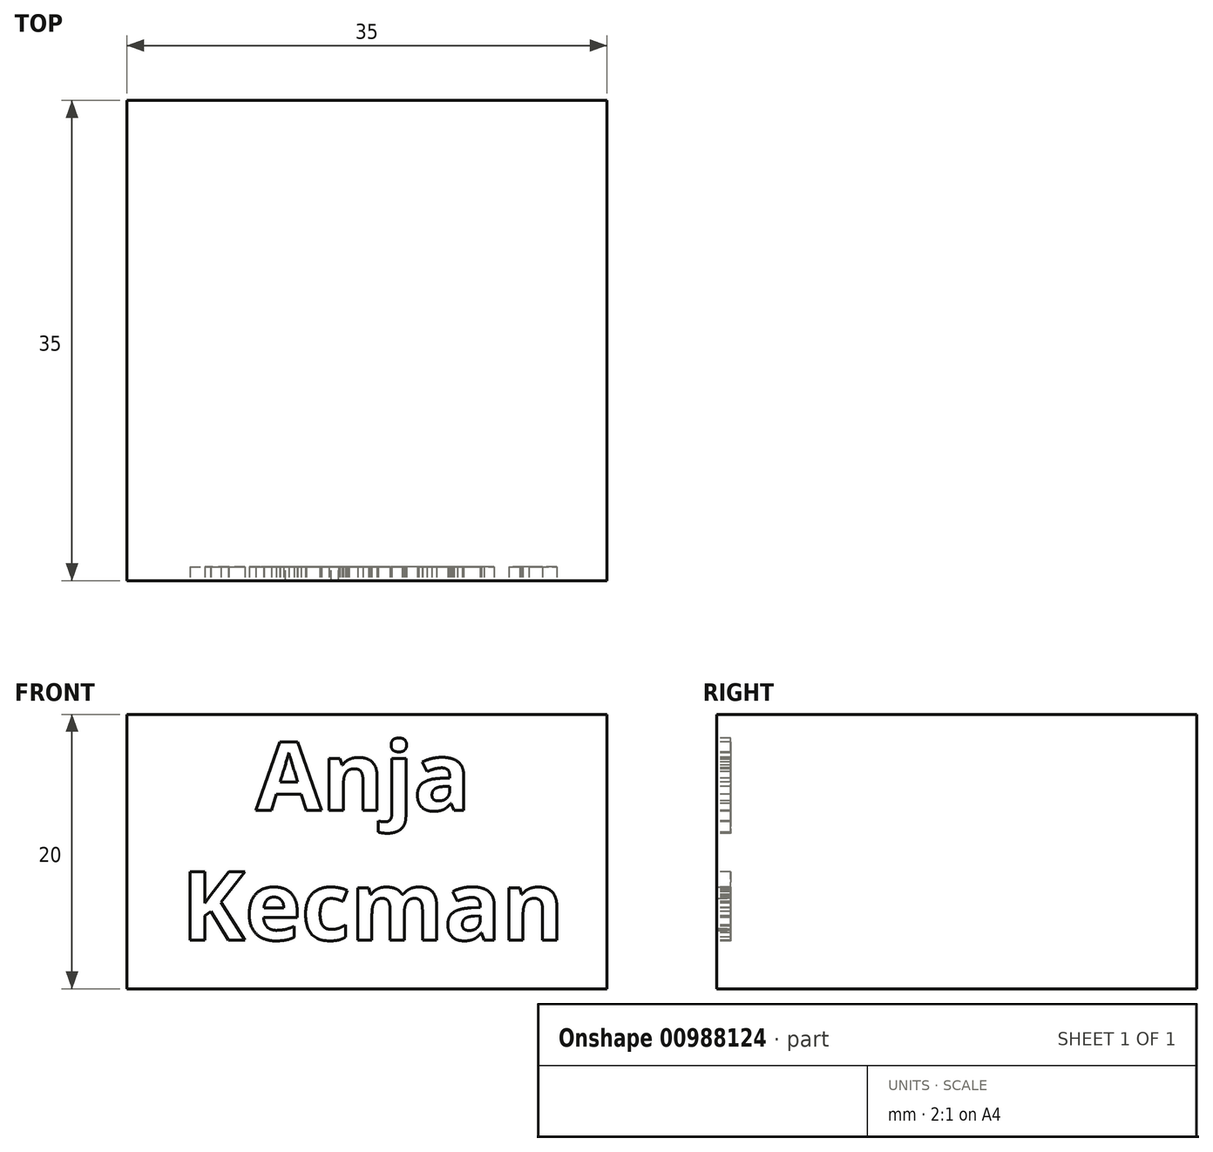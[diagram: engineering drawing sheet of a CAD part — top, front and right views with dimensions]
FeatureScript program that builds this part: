
annotation { "Feature Type Name" : "Feature", "Feature Type Description" : "" }
export const myFeature = defineFeature(function(context is Context, id is Id, definition is map)
    precondition{}
    {
        {
            var Q0;
            Q0=qCreatedBy(makeId("Top.planeOp"),FACE);
            var sketch = newSketch(context, id + "F0", { "sketchPlane" : qUnion([Q0])});
            skLineSegment(sketch, "E0.bottom", {"start": v(0, 0) * mm, "end": v(35, 0) * mm});
            skLineSegment(sketch, "E0.top", {"start": v(0, 35) * mm, "end": v(35, 35) * mm});
            skLineSegment(sketch, "E0.left", {"start": v(0, 0) * mm, "end": v(0, 35) * mm});
            skLineSegment(sketch, "E0.right", {"start": v(35, 0) * mm, "end": v(35, 35) * mm});
            skSolve(sketch);
        }
        {
            var Q0;
            Q0 = qSketchRegion(id + "F0", true);
            extrude(context, id + "F1", {"entities" : qUnion([Q0]), "depth" : 20 * mm, "offsetDistance" : 25 * mm});
        }
        {
            var Q0;
            Q0=makeQuery(id+"F1.opExtrude","SWEPT_FACE",FACE,{"disambiguationData":[OSD([sQuery(id+"F0.wireOp",EDGE,"E0.bottom")])]});
            var sketch = newSketch(context, id + "F2", { "sketchPlane" : qUnion([Q0])});
            skText(sketch, "E1", { "text": "   Anja\nKecman", "fontName": "OpenSans-Bold.ttf"});
            const initialGuessF2  = {"E1": [0.004, 0.013, 1, 0, 0.005]};
            skSetInitialGuess(sketch, initialGuessF2);
            skSolve(sketch);
        }
        {
            var Q0;
            Q0 = qSketchRegion(id + "F2", true);
            extrude(context, id + "F3", {"entities" : qUnion([Q0]), "operationType" : NewBodyOperationType.REMOVE, "oppositeDirection" : true, "depth" : 1 * mm, "offsetDistance" : 25 * mm});
        }
    });
